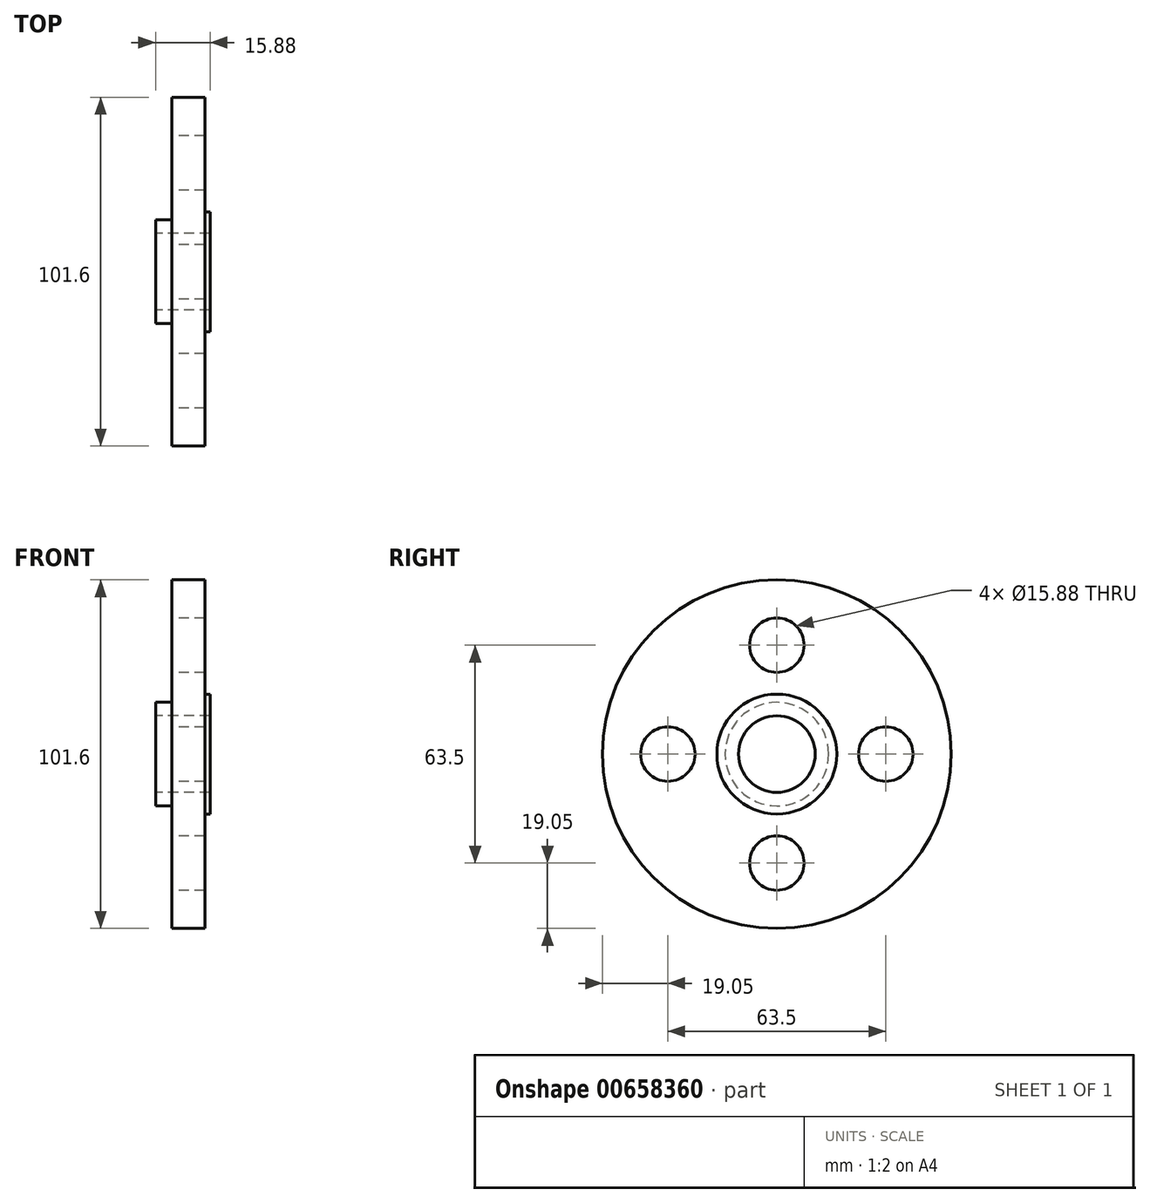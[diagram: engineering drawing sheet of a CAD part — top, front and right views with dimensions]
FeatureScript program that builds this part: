
annotation { "Feature Type Name" : "Feature", "Feature Type Description" : "" }
export const myFeature = defineFeature(function(context is Context, id is Id, definition is map)
    precondition{}
    {
        {
            var Q0;
            Q0=qCreatedBy(makeId("Front.planeOp"),FACE);
            var sketch = newSketch(context, id + "F0", { "sketchPlane" : qUnion([Q0])});
            skLineSegment(sketch, "E0", {"start": v(-18.14, 0) * mm, "end": v(21.74, 0) * mm, "construction": true});
            skLineSegment(sketch, "E1", {"start": v(1.12, 11.18) * mm, "end": v(17, 11.18) * mm});
            skLineSegment(sketch, "E2", {"start": v(17, 11.18) * mm, "end": v(17, 17.46) * mm});
            skLineSegment(sketch, "E3", {"start": v(17, 17.46) * mm, "end": v(15.47, 17.46) * mm});
            skLineSegment(sketch, "E4", {"start": v(15.47, 17.46) * mm, "end": v(15.47, 50.8) * mm});
            skLineSegment(sketch, "E5", {"start": v(15.47, 50.8) * mm, "end": v(5.9, 50.8) * mm});
            skLineSegment(sketch, "E6", {"start": v(5.9, 50.8) * mm, "end": v(5.9, 15.09) * mm});
            skLineSegment(sketch, "E7", {"start": v(5.9, 15.09) * mm, "end": v(1.12, 15.09) * mm});
            skLineSegment(sketch, "E8", {"start": v(1.12, 15.09) * mm, "end": v(1.12, 11.18) * mm});
            skSolve(sketch);
        }
        {
            var Q0;
            Q0=makeQuery(id+"F0.imprint","IMPRINT",FACE,{"disambiguationData":[TD([[makeQuery(id+"F0.imprint","IMPRINT",EDGE,{"derivedFrom":sQuery(id+"F0.wireOp",EDGE,"E1")}),1.0]])]});
            var Q1;
            Q1=sQuery(id+"F0.wireOp",EDGE,"E0");
            revolve(context, id + "F1", {"entities" : qUnion([Q0]), "axis" : qUnion([Q1]), "revolveType" : RevolveType.FULL});
        }
        {
            var Q0;
            Q0=makeQuery(id+"F1.opRevolve","SWEPT_FACE",FACE,{"disambiguationData":[OSD([sQuery(id+"F0.wireOp",EDGE,"E6")])]});
            var sketch = newSketch(context, id + "F2", { "sketchPlane" : qUnion([Q0])});
            skCircle(sketch, "E9", {"center": v(0, 0) * mm, "radius": 31.75 * mm, "construction": true});
            skCircle(sketch, "E10", {"center": v(0, 31.75) * mm, "radius": 7.94 * mm});
            skCircle(sketch, "E11.1.0", {"center": v(-31.75, 0) * mm, "radius": 7.94 * mm});
            skCircle(sketch, "E11.2.0", {"center": v(0, -31.75) * mm, "radius": 7.94 * mm});
            skCircle(sketch, "E11.3.0", {"center": v(31.75, 0) * mm, "radius": 7.94 * mm});
            skSolve(sketch);
        }
        {
            var Q0;
            Q0 = qSketchRegion(id + "F2", true);
            extrude(context, id + "F3", {"entities" : qUnion([Q0]), "operationType" : NewBodyOperationType.REMOVE, "oppositeDirection" : true, "depth" : 37.85 * mm, "offsetDistance" : 25.4 * mm});
        }
    });
